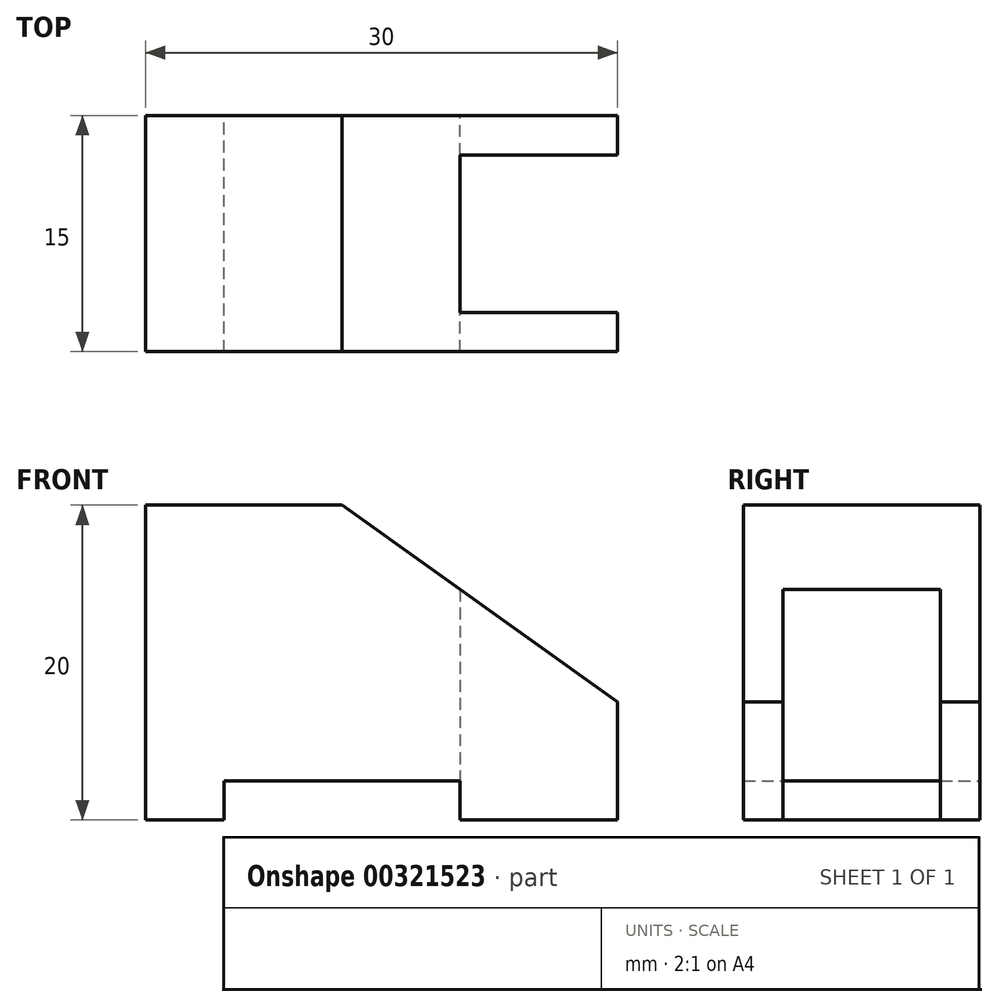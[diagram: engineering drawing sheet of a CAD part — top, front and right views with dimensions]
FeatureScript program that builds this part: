
annotation { "Feature Type Name" : "Feature", "Feature Type Description" : "" }
export const myFeature = defineFeature(function(context is Context, id is Id, definition is map)
    precondition{}
    {
        {
            var Q0;
            Q0=qCreatedBy(makeId("Front.planeOp"),FACE);
            var sketch = newSketch(context, id + "F0", { "sketchPlane" : qUnion([Q0])});
            skLineSegment(sketch, "E0", {"start": v(0, 0) * mm, "end": v(0, 20) * mm});
            skLineSegment(sketch, "E1", {"start": v(0, 20) * mm, "end": v(12.5, 20) * mm});
            skLineSegment(sketch, "E2", {"start": v(0, 0) * mm, "end": v(5, 0) * mm});
            skLineSegment(sketch, "E3", {"start": v(5, 0) * mm, "end": v(5, 2.5) * mm});
            skLineSegment(sketch, "E4", {"start": v(5, 2.5) * mm, "end": v(20, 2.5) * mm});
            skLineSegment(sketch, "E5", {"start": v(20, 2.5) * mm, "end": v(20, 0) * mm});
            skLineSegment(sketch, "E6", {"start": v(20, 0) * mm, "end": v(30, 0) * mm});
            skLineSegment(sketch, "E7", {"start": v(30, 0) * mm, "end": v(30, 7.5) * mm});
            skLineSegment(sketch, "E8", {"start": v(30, 7.5) * mm, "end": v(12.5, 20) * mm});
            skSolve(sketch);
        }
        {
            var Q0;
            Q0=makeQuery(id+"F0.imprint","IMPRINT",FACE,{"disambiguationData":[TD([[makeQuery(id+"F0.imprint","IMPRINT",EDGE,{"derivedFrom":sQuery(id+"F0.wireOp",EDGE,"E0")}),-1.0]])]});
            extrude(context, id + "F1", {"entities" : qUnion([Q0]), "depth" : 15 * mm});
        }
        {
            var Q0;
            Q0=makeQuery(id+"F1.opExtrude","SWEPT_FACE",FACE,{"disambiguationData":[OSD([sQuery(id+"F0.wireOp",EDGE,"E6")])]});
            var sketch = newSketch(context, id + "F2", { "sketchPlane" : qUnion([Q0])});
            skLineSegment(sketch, "E9.bottom", {"start": v(30, 12.5) * mm, "end": v(20, 12.5) * mm});
            skLineSegment(sketch, "E9.top", {"start": v(30, 2.5) * mm, "end": v(20, 2.5) * mm});
            skLineSegment(sketch, "E9.left", {"start": v(30, 12.5) * mm, "end": v(30, 2.5) * mm});
            skLineSegment(sketch, "E9.right", {"start": v(20, 12.5) * mm, "end": v(20, 2.5) * mm});
            skSolve(sketch);
        }
        {
            var Q0;
            Q0=makeQuery(id+"F2.imprint","IMPRINT",FACE,{"disambiguationData":[TD([[makeQuery(id+"F2.imprint","IMPRINT",EDGE,{"derivedFrom":sQuery(id+"F2.wireOp",EDGE,"E9.bottom")}),1.0]])]});
            extrude(context, id + "F3", {"entities" : qUnion([Q0]), "operationType" : NewBodyOperationType.REMOVE, "endBound" : BoundingType.THROUGH_ALL, "oppositeDirection" : true, "depth" : 25 * mm});
        }
    });
